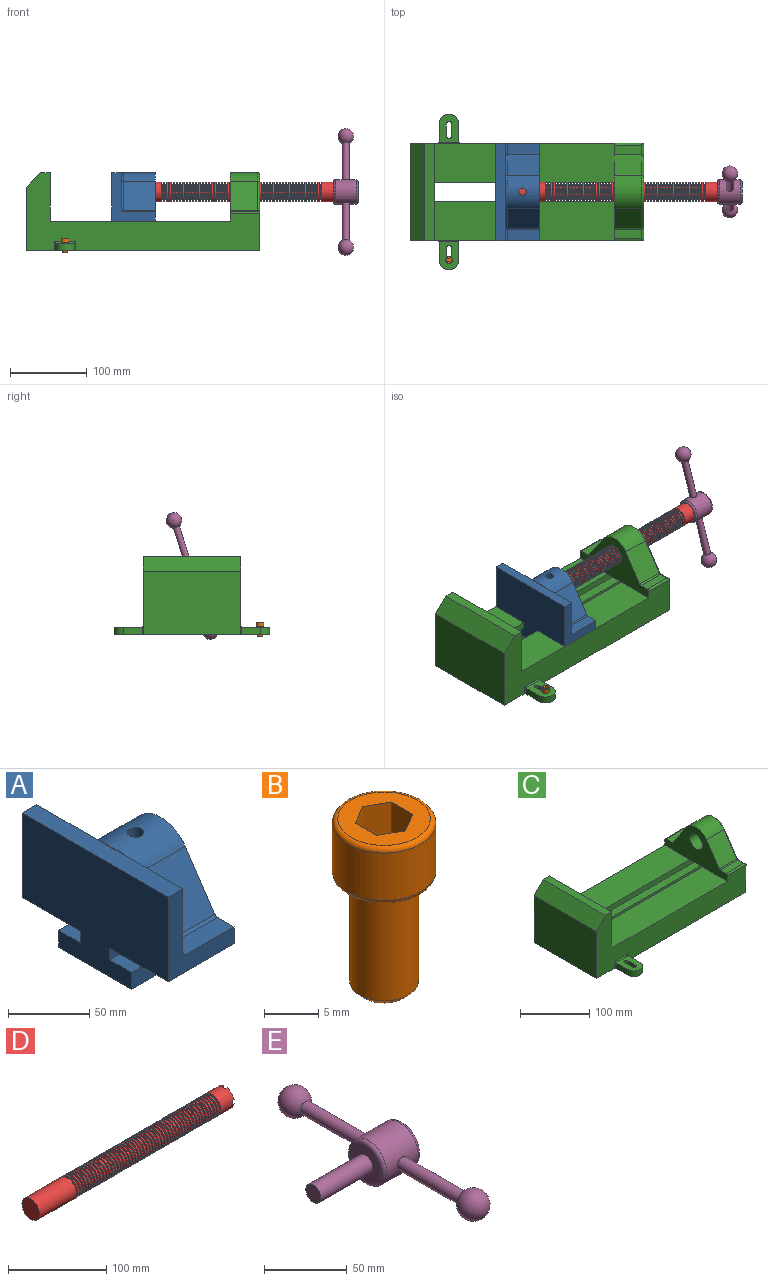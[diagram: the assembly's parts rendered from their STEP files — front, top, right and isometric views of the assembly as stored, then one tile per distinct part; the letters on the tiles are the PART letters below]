
ASSEMBLY  parts=5 mates=5
PART A: 36 faces, bbox 57.2x127x89 mm
  f0: plane 57.15x50.8mm, normal (0,0,-1), area 2903.2mm2, adj f6,f9,f10,f23
  f1: cylinder r=12.7mm len=44.45mm, axis (1,0,0), area 3464.3mm2, adj f6,f15,f16
  f2: plane 41.91x14.52mm, normal (0,0,1), area 608.5mm2, adj f6,f11,f24,f25
  f3: plane 51.86x48.26mm, normal (1,0,0), area 1495.7mm2, adj f8,f10,f31,f33,f35
  f4: plane 51.86x48.26mm, normal (1,0,0), area 1495.7mm2, adj f8,f11,f24,f28,f29
  f5: plane 57.15x50.8mm, normal (0,0,-1), area 2903.2mm2, adj f6,f9,f11,f22
  f6: plane 127x85.09mm, normal (1,0,0), area 5190.6mm2, adj f0,f1,f2,f5,f7,f10,f11,f12
  f7: plane 41.91x14.52mm, normal (0,0,1), area 608.5mm2, adj f6,f10,f30,f31
  f8: plane 127x12.7mm, normal (0,0,1), area 1612.9mm2, adj f3,f4,f9,f10,f11,f26,f34
  f9: plane 127x85.09mm, normal (-1,0,0), area 9096.8mm2, adj f0,f5,f8,f10,f11,f17,f18,f19
  f10: plane 63.5x57.15mm, normal (0,-1,0), area 1372.3mm2, adj f0,f3,f6,f7,f8,f9,f31
  f11: plane 63.5x57.15mm, normal (0,1,0), area 1372.3mm2, adj f2,f4,f5,f6,f8,f9,f24
  f12: plane 41.91x38.43mm, normal (0,-0.83,0.56), area 1939.2mm2, adj f6,f13,f30,f33
  f13: cylinder r=25.4mm len=44.45mm, axis (1,0,0), area 2026.5mm2, adj f6,f12,f14,f16,f26,f28,f34,f35
  f14: plane 41.91x38.43mm, normal (0,0.83,0.56), area 1939.2mm2, adj f6,f13,f25,f29
  f15: plane 25.4x25.4mm, normal (1,0,0), area 506.7mm2, adj f1
  f16: cylinder r=5.08mm len=13.76mm, axis (0,0,1), area 414mm2, adj f1,f13
  f17: plane 57.15x19.05mm, normal (0,0,1), area 1088.7mm2, adj f6,f9,f18,f23
  f18: plane 57.15x12.7mm, normal (0,-1,0), area 725.8mm2, adj f6,f9,f17,f19
  f19: plane 63.5x57.15mm, normal (0,0,-1), area 3629mm2, adj f6,f9,f18,f20
  f20: plane 57.15x12.7mm, normal (0,1,0), area 725.8mm2, adj f6,f9,f19,f21
  f21: plane 57.15x19.05mm, normal (0,0,1), area 1088.7mm2, adj f6,f9,f20,f22
  f22: plane 57.15x8.89mm, normal (0,1,0), area 508.1mm2, adj f5,f6,f9,f21
  f23: plane 57.15x8.89mm, normal (0,-1,0), area 508.1mm2, adj f0,f6,f9,f17
  f24: cylinder r=2.54mm len=14.52mm, axis (0,-1,0), area 57.9mm2, adj f2,f4,f11,f27
  f25: cylinder r=2.54mm len=41.91mm, axis (1,0,0), area 104.3mm2, adj f2,f6,f14,f27
  f26: bspline ~12.24x2.8mm, area 20.9mm2, adj f8,f13,f28
  f27: sphere r=2.54mm, area 6.3mm2, adj f24,f25,f29
  f28: torus R=27.94mm, axis (1,0,0), area 57.8mm2, adj f4,f13,f26,f29
  f29: cylinder r=2.54mm len=39.84mm, axis (0,-0.56,0.83), area 184.6mm2, adj f4,f14,f27,f28
  f30: cylinder r=2.54mm len=41.91mm, axis (1,0,0), area 104.3mm2, adj f6,f7,f12,f32
  f31: cylinder r=2.54mm len=14.52mm, axis (0,-1,0), area 57.9mm2, adj f3,f7,f10,f32
  f32: sphere r=2.54mm, area 6.3mm2, adj f30,f31,f33
  f33: cylinder r=2.54mm len=39.84mm, axis (0,-0.56,-0.83), area 184.6mm2, adj f3,f12,f32,f35
  f34: bspline ~12.24x2.8mm, area 20.9mm2, adj f8,f13,f35
  f35: torus R=27.94mm, axis (1,0,0), area 57.8mm2, adj f3,f13,f33,f34
PART B: 15 faces, bbox 10.3x10.3x19.1 mm
  f0: plane 8.51x8.51mm, normal (0,0,1), area 37.2mm2, adj f5,f6,f7,f8,f9,f10,f14
  f1: cylinder r=3.17mm len=11.94mm, axis (0,0,1), area 238.2mm2, adj f4,f12
  f2: plane 4.83x4.83mm, normal (0,0,-1), area 18.3mm2, adj f12
  f3: cylinder r=4.76mm len=9.53mm, axis (0,0,-1), area 159.6mm2, adj f13,f14
  f4: plane 8.51x8.51mm, normal (0,0,-1), area 25.2mm2, adj f1,f13
  f5: plane 4.83x2.38mm, normal (-0.5,-0.87,0), area 13.3mm2, adj f0,f6,f10,f11
  f6: plane 4.83x2.38mm, normal (0.5,-0.87,0), area 13.3mm2, adj f0,f5,f7,f11
  f7: plane 4.83x2.75mm, normal (1,0,0), area 13.3mm2, adj f0,f6,f8,f11
  f8: plane 4.83x2.38mm, normal (0.5,0.87,0), area 13.3mm2, adj f0,f7,f9,f11
  f9: plane 4.83x2.38mm, normal (-0.5,0.87,0), area 13.3mm2, adj f0,f8,f10,f11
  f10: plane 4.83x2.75mm, normal (-1,0,0), area 13.3mm2, adj f0,f5,f9,f11
  f11: plane 5.5x4.76mm, normal (0,0,1), area 19.6mm2, adj f5,f6,f7,f8,f9,f10
  f12: cone r=3.17mm half-angle=45deg, axis (0,0,1), area 18.9mm2, adj f1,f2
  f13: torus R=4.25mm, axis (0,0,1), area 23mm2, adj f3,f4
  f14: torus R=4.25mm, axis (0,0,1), area 23mm2, adj f0,f3
PART C: 61 faces, bbox 304.8x203.2x103.7 mm
  f0: plane 304.8x101.6mm, normal (0,1,0), area 13520.3mm2, adj f3,f4,f5,f6,f7,f8,f9,f16
  f1: plane 304.8x101.6mm, normal (0,-1,0), area 13520.3mm2, adj f2,f3,f5,f6,f7,f8,f9,f16
  f2: plane 234.95x50.8mm, normal (0,0,1), area 11935.5mm2, adj f1,f5,f16,f26
  f3: plane 127x99.06mm, normal (1,0,0), area 7097.5mm2, adj f0,f1,f9,f14,f17,f18,f19,f20
  f4: plane 234.95x50.8mm, normal (0,0,1), area 11935.5mm2, adj f0,f5,f16,f27
  f5: plane 127x101.6mm, normal (1,0,0), area 9516.1mm2, adj f0,f1,f2,f4,f6,f9,f18,f19
  f6: plane 127x12.7mm, normal (0,0,1), area 1612.9mm2, adj f0,f1,f5,f7
  f7: plane 127x19.05mm, normal (-0.71,0,0.71), area 3421.5mm2, adj f0,f1,f6,f8
  f8: plane 127x82.55mm, normal (-1,0,0), area 10483.8mm2, adj f0,f1,f7,f9
  f9: plane 304.8x203.2mm, normal (0,0,-1), area 33298.3mm2, adj f0,f1,f3,f5,f8,f21,f22,f39
  f10: plane 35.56x11.98mm, normal (0,0,1), area 426mm2, adj f16,f28,f29,f30
  f11: plane 38.43x35.56mm, normal (0,0.83,0.56), area 1645.4mm2, adj f12,f16,f29,f32
  f12: cylinder r=25.4mm len=42.19mm, axis (1,0,0), area 1770.2mm2, adj f11,f13,f16,f33
  f13: plane 38.43x35.56mm, normal (0,-0.83,0.56), area 1645.4mm2, adj f12,f16,f34,f35
  f14: cylinder r=12.7mm len=38.1mm, axis (1,0,0), area 3040.2mm2, adj f3,f16
  f15: plane 35.56x11.98mm, normal (0,0,1), area 426mm2, adj f16,f34,f36,f38
  f16: plane 127x63.5mm, normal (-1,0,0), area 4155.5mm2, adj f0,f1,f2,f4,f10,f11,f12,f13
  f17: plane 38.1x25.4mm, normal (0,0,-1), area 967.7mm2, adj f3,f16,f26,f27
  f18: plane 273.05x19.05mm, normal (0,0,-1), area 5201.6mm2, adj f3,f5,f19,f26
  f19: plane 273.05x12.7mm, normal (0,1,0), area 3467.7mm2, adj f3,f5,f18,f20
  f20: plane 273.05x19.05mm, normal (0,0,1), area 5201.6mm2, adj f3,f5,f19,f21
  f21: plane 273.05x16.51mm, normal (0,1,0), area 4508.1mm2, adj f3,f5,f9,f20
  f22: plane 273.05x16.51mm, normal (0,-1,0), area 4508.1mm2, adj f3,f5,f9,f23
  f23: plane 273.05x19.05mm, normal (0,0,1), area 5201.6mm2, adj f3,f5,f22,f24
  f24: plane 273.05x12.7mm, normal (0,-1,0), area 3467.7mm2, adj f3,f5,f23,f25
  f25: plane 273.05x19.05mm, normal (0,0,-1), area 5201.6mm2, adj f3,f5,f24,f27
  f26: plane 273.05x8.89mm, normal (0,1,0), area 2427.4mm2, adj f2,f3,f5,f17,f18
  f27: plane 273.05x8.89mm, normal (0,-1,0), area 2427.4mm2, adj f3,f4,f5,f17,f25
  f28: cylinder r=2.54mm len=38.1mm, axis (1,0,0), area 148.3mm2, adj f0,f10,f16,f30
  f29: cylinder r=2.54mm len=35.56mm, axis (-1,0,0), area 88.5mm2, adj f10,f11,f16,f31
  f30: cylinder r=2.54mm len=14.52mm, axis (0,1,0), area 54.3mm2, adj f3,f10,f28,f31
  f31: torus R=5.08mm, axis (-1,0,0), area 13.5mm2, adj f3,f29,f30,f32
  f32: cylinder r=2.54mm len=39.84mm, axis (0,0.56,-0.83), area 184.6mm2, adj f3,f11,f31,f33
  f33: torus R=22.86mm, axis (-1,0,0), area 191.4mm2, adj f3,f12,f32,f35
  f34: cylinder r=2.54mm len=35.56mm, axis (-1,0,0), area 88.5mm2, adj f13,f15,f16,f37
  f35: cylinder r=2.54mm len=39.84mm, axis (0,0.56,0.83), area 184.6mm2, adj f3,f13,f33,f37
  f36: cylinder r=2.54mm len=38.1mm, axis (-1,0,0), area 148.3mm2, adj f1,f15,f16,f38
  f37: torus R=5.08mm, axis (-1,0,0), area 13.5mm2, adj f3,f34,f35,f38
  f38: cylinder r=2.54mm len=14.52mm, axis (0,1,0), area 54.3mm2, adj f3,f15,f36,f37
  f39: plane 23.88x9.53mm, normal (-1,0,0), area 227.4mm2, adj f9,f45,f46,f60
  f40: plane 23.88x9.53mm, normal (1,0,0), area 227.4mm2, adj f9,f45,f46,f58
  f41: cylinder r=3.3mm len=9.53mm, axis (0,0,-1), area 98.8mm2, adj f9,f42,f44,f46
  f42: plane 15.62x9.53mm, normal (-1,0,0), area 148.8mm2, adj f9,f41,f43,f46
  f43: cylinder r=3.3mm len=9.53mm, axis (0,0,-1), area 98.8mm2, adj f9,f42,f44,f46
  f44: plane 15.62x9.53mm, normal (1,0,0), area 148.8mm2, adj f9,f41,f43,f46
  f45: cylinder r=12.7mm len=25.4mm, axis (0,0,-1), area 380mm2, adj f9,f39,f40,f46
  f46: plane 36.58x25.4mm, normal (0,0,1), area 722.4mm2, adj f39,f40,f41,f42,f43,f44,f45,f59
  f47: plane 23.88x9.53mm, normal (-1,0,0), area 227.4mm2, adj f9,f53,f54,f56
  f48: plane 23.88x9.53mm, normal (1,0,0), area 227.4mm2, adj f9,f53,f54,f55
  f49: cylinder r=3.3mm len=9.53mm, axis (0,0,-1), area 98.8mm2, adj f9,f50,f52,f54
  f50: plane 15.62x9.53mm, normal (-1,0,0), area 148.8mm2, adj f9,f49,f51,f54
  f51: cylinder r=3.3mm len=9.53mm, axis (0,0,-1), area 98.8mm2, adj f9,f50,f52,f54
  f52: plane 15.62x9.53mm, normal (1,0,0), area 148.8mm2, adj f9,f49,f51,f54
  f53: cylinder r=12.7mm len=25.4mm, axis (0,0,-1), area 380mm2, adj f9,f47,f48,f54
  f54: plane 36.58x25.4mm, normal (0,0,1), area 722.4mm2, adj f47,f48,f49,f50,f51,f52,f53,f57
  f55: cylinder r=1.52mm len=11.05mm, axis (0,0,-1), area 24.1mm2, adj f0,f9,f48,f57
  f56: cylinder r=1.52mm len=11.05mm, axis (0,0,1), area 24.1mm2, adj f0,f9,f47,f57
  f57: cylinder r=1.52mm len=28.45mm, axis (1,0,0), area 63.5mm2, adj f0,f54,f55,f56
  f58: cylinder r=1.52mm len=11.05mm, axis (0,0,1), area 24.1mm2, adj f1,f9,f40,f59
  f59: cylinder r=1.52mm len=28.45mm, axis (-1,0,0), area 63.5mm2, adj f1,f46,f58,f60
  f60: cylinder r=1.52mm len=11.05mm, axis (0,0,-1), area 24.1mm2, adj f1,f9,f39,f59
PART D: 220 faces, bbox 279.4x25.4x25.4 mm
  f0: cylinder r=12.7mm len=25.4mm, axis (-1,0,0), area 1468.2mm2, adj f1,f2,f3,f5,f7,f208,f209,f210
  f1: plane 9.9x9.9mm, normal (1,0,0), area 62.3mm2, adj f0,f4,f213,f216
  f2: plane 9.9x9.9mm, normal (1,0,0), area 62.3mm2, adj f0,f4,f210,f218
  f3: plane 9.9x9.9mm, normal (1,0,0), area 62.3mm2, adj f0,f4,f209,f212
  f4: cylinder r=6.35mm len=25.4mm, axis (1,0,0), area 960.3mm2, adj f1,f2,f3,f5,f6,f208,f209,f210
  f5: plane 9.9x9.9mm, normal (1,0,0), area 62.3mm2, adj f0,f4,f215,f217
  f6: plane 12.7x12.7mm, normal (1,0,0), area 126.7mm2, adj f4
  f7: cone r=12.7mm half-angle=76deg, axis (1,0,0), area 188mm2, adj f0,f9
  f8: cone r=10.16mm half-angle=76deg, axis (-1,0,0), area 188mm2, adj f9,f10
  f9: cylinder r=10.16mm len=20.32mm, axis (1,0,0), area 81.1mm2, adj f7,f8
  f10: cylinder r=12.7mm len=25.4mm, axis (-1,0,0), area 131.7mm2, adj f8,f11
  f11: cone r=12.7mm half-angle=76deg, axis (1,0,0), area 188mm2, adj f10,f13
  f12: cone r=10.16mm half-angle=76deg, axis (-1,0,0), area 188mm2, adj f13,f14
  f13: cylinder r=10.16mm len=20.32mm, axis (1,0,0), area 81.1mm2, adj f11,f12
  f14: cylinder r=12.7mm len=25.4mm, axis (-1,0,0), area 131.7mm2, adj f12,f15
  f15: cone r=12.7mm half-angle=76deg, axis (1,0,0), area 188mm2, adj f14,f17
  f16: cone r=10.16mm half-angle=76deg, axis (-1,0,0), area 188mm2, adj f17,f18
  f17: cylinder r=10.16mm len=20.32mm, axis (1,0,0), area 81.1mm2, adj f15,f16
  f18: cylinder r=12.7mm len=25.4mm, axis (-1,0,0), area 131.7mm2, adj f16,f19
  f19: cone r=12.7mm half-angle=76deg, axis (1,0,0), area 188mm2, adj f18,f21
  f20: cone r=10.16mm half-angle=76deg, axis (-1,0,0), area 188mm2, adj f21,f22
  f21: cylinder r=10.16mm len=20.32mm, axis (1,0,0), area 81.1mm2, adj f19,f20
  f22: cylinder r=12.7mm len=25.4mm, axis (-1,0,0), area 131.7mm2, adj f20,f23
  f23: cone r=12.7mm half-angle=76deg, axis (1,0,0), area 188mm2, adj f22,f25
  f24: cone r=10.16mm half-angle=76deg, axis (-1,0,0), area 188mm2, adj f25,f26
  f25: cylinder r=10.16mm len=20.32mm, axis (1,0,0), area 81.1mm2, adj f23,f24
  f26: cylinder r=12.7mm len=25.4mm, axis (-1,0,0), area 131.7mm2, adj f24,f27
  f27: cone r=12.7mm half-angle=76deg, axis (1,0,0), area 188mm2, adj f26,f29
  f28: cone r=10.16mm half-angle=76deg, axis (-1,0,0), area 188mm2, adj f29,f30
  f29: cylinder r=10.16mm len=20.32mm, axis (1,0,0), area 81.1mm2, adj f27,f28
  f30: cylinder r=12.7mm len=25.4mm, axis (-1,0,0), area 131.7mm2, adj f28,f31
  f31: cone r=12.7mm half-angle=76deg, axis (1,0,0), area 188mm2, adj f30,f33
  f32: cone r=10.16mm half-angle=76deg, axis (-1,0,0), area 188mm2, adj f33,f34
  f33: cylinder r=10.16mm len=20.32mm, axis (1,0,0), area 81.1mm2, adj f31,f32
  f34: cylinder r=12.7mm len=25.4mm, axis (-1,0,0), area 131.7mm2, adj f32,f35
  f35: cone r=12.7mm half-angle=76deg, axis (1,0,0), area 188mm2, adj f34,f37
  f36: cone r=10.16mm half-angle=76deg, axis (-1,0,0), area 188mm2, adj f37,f38
  f37: cylinder r=10.16mm len=20.32mm, axis (1,0,0), area 81.1mm2, adj f35,f36
  f38: cylinder r=12.7mm len=25.4mm, axis (-1,0,0), area 131.7mm2, adj f36,f39
  f39: cone r=12.7mm half-angle=76deg, axis (1,0,0), area 188mm2, adj f38,f41
  f40: cone r=10.16mm half-angle=76deg, axis (-1,0,0), area 188mm2, adj f41,f42
  f41: cylinder r=10.16mm len=20.32mm, axis (1,0,0), area 81.1mm2, adj f39,f40
  f42: cylinder r=12.7mm len=25.4mm, axis (-1,0,0), area 131.7mm2, adj f40,f43
  f43: cone r=12.7mm half-angle=76deg, axis (1,0,0), area 188mm2, adj f42,f45
  f44: cone r=10.16mm half-angle=76deg, axis (-1,0,0), area 188mm2, adj f45,f46
  f45: cylinder r=10.16mm len=20.32mm, axis (1,0,0), area 81.1mm2, adj f43,f44
  f46: cylinder r=12.7mm len=25.4mm, axis (-1,0,0), area 131.7mm2, adj f44,f47
  f47: cone r=12.7mm half-angle=76deg, axis (1,0,0), area 188mm2, adj f46,f49
  f48: cone r=10.16mm half-angle=76deg, axis (-1,0,0), area 188mm2, adj f49,f50
  f49: cylinder r=10.16mm len=20.32mm, axis (1,0,0), area 81.1mm2, adj f47,f48
  f50: cylinder r=12.7mm len=25.4mm, axis (-1,0,0), area 131.7mm2, adj f48,f51
  f51: cone r=12.7mm half-angle=76deg, axis (1,0,0), area 188mm2, adj f50,f53
  f52: cone r=10.16mm half-angle=76deg, axis (-1,0,0), area 188mm2, adj f53,f54
  f53: cylinder r=10.16mm len=20.32mm, axis (1,0,0), area 81.1mm2, adj f51,f52
  f54: cylinder r=12.7mm len=25.4mm, axis (-1,0,0), area 131.7mm2, adj f52,f55
  f55: cone r=12.7mm half-angle=76deg, axis (1,0,0), area 188mm2, adj f54,f57
  f56: cone r=10.16mm half-angle=76deg, axis (-1,0,0), area 188mm2, adj f57,f58
  f57: cylinder r=10.16mm len=20.32mm, axis (1,0,0), area 81.1mm2, adj f55,f56
  f58: cylinder r=12.7mm len=25.4mm, axis (-1,0,0), area 131.7mm2, adj f56,f59
  f59: cone r=12.7mm half-angle=76deg, axis (1,0,0), area 188mm2, adj f58,f61
  f60: cone r=10.16mm half-angle=76deg, axis (-1,0,0), area 188mm2, adj f61,f62
  f61: cylinder r=10.16mm len=20.32mm, axis (1,0,0), area 81.1mm2, adj f59,f60
  f62: cylinder r=12.7mm len=25.4mm, axis (-1,0,0), area 131.7mm2, adj f60,f63
  f63: cone r=12.7mm half-angle=76deg, axis (1,0,0), area 188mm2, adj f62,f65
  f64: cone r=10.16mm half-angle=76deg, axis (-1,0,0), area 188mm2, adj f65,f66
  f65: cylinder r=10.16mm len=20.32mm, axis (1,0,0), area 81.1mm2, adj f63,f64
  f66: cylinder r=12.7mm len=25.4mm, axis (-1,0,0), area 131.7mm2, adj f64,f67
  f67: cone r=12.7mm half-angle=76deg, axis (1,0,0), area 188mm2, adj f66,f69
  f68: cone r=10.16mm half-angle=76deg, axis (-1,0,0), area 188mm2, adj f69,f70
  f69: cylinder r=10.16mm len=20.32mm, axis (1,0,0), area 81.1mm2, adj f67,f68
  f70: cylinder r=12.7mm len=25.4mm, axis (-1,0,0), area 131.7mm2, adj f68,f71
  f71: cone r=12.7mm half-angle=76deg, axis (1,0,0), area 188mm2, adj f70,f73
  f72: cone r=10.16mm half-angle=76deg, axis (-1,0,0), area 188mm2, adj f73,f74
  f73: cylinder r=10.16mm len=20.32mm, axis (1,0,0), area 81.1mm2, adj f71,f72
  f74: cylinder r=12.7mm len=25.4mm, axis (-1,0,0), area 131.7mm2, adj f72,f75
  f75: cone r=12.7mm half-angle=76deg, axis (1,0,0), area 188mm2, adj f74,f77
  f76: cone r=10.16mm half-angle=76deg, axis (-1,0,0), area 188mm2, adj f77,f78
  f77: cylinder r=10.16mm len=20.32mm, axis (1,0,0), area 81.1mm2, adj f75,f76
  f78: cylinder r=12.7mm len=25.4mm, axis (-1,0,0), area 131.7mm2, adj f76,f79
  f79: cone r=12.7mm half-angle=76deg, axis (1,0,0), area 188mm2, adj f78,f81
  f80: cone r=10.16mm half-angle=76deg, axis (-1,0,0), area 188mm2, adj f81,f82
  f81: cylinder r=10.16mm len=20.32mm, axis (1,0,0), area 81.1mm2, adj f79,f80
  f82: cylinder r=12.7mm len=25.4mm, axis (-1,0,0), area 131.7mm2, adj f80,f83
  f83: cone r=12.7mm half-angle=76deg, axis (1,0,0), area 188mm2, adj f82,f85
  f84: cone r=10.16mm half-angle=76deg, axis (-1,0,0), area 188mm2, adj f85,f86
  f85: cylinder r=10.16mm len=20.32mm, axis (1,0,0), area 81.1mm2, adj f83,f84
  f86: cylinder r=12.7mm len=25.4mm, axis (-1,0,0), area 131.7mm2, adj f84,f87
  f87: cone r=12.7mm half-angle=76deg, axis (1,0,0), area 188mm2, adj f86,f89
  f88: cone r=10.16mm half-angle=76deg, axis (-1,0,0), area 188mm2, adj f89,f90
  f89: cylinder r=10.16mm len=20.32mm, axis (1,0,0), area 81.1mm2, adj f87,f88
  f90: cylinder r=12.7mm len=25.4mm, axis (-1,0,0), area 131.7mm2, adj f88,f91
  f91: cone r=12.7mm half-angle=76deg, axis (1,0,0), area 188mm2, adj f90,f93
  f92: cone r=10.16mm half-angle=76deg, axis (-1,0,0), area 188mm2, adj f93,f94
  f93: cylinder r=10.16mm len=20.32mm, axis (1,0,0), area 81.1mm2, adj f91,f92
  f94: cylinder r=12.7mm len=25.4mm, axis (-1,0,0), area 131.7mm2, adj f92,f95
  f95: cone r=12.7mm half-angle=76deg, axis (1,0,0), area 188mm2, adj f94,f97
  f96: cone r=10.16mm half-angle=76deg, axis (-1,0,0), area 188mm2, adj f97,f98
  f97: cylinder r=10.16mm len=20.32mm, axis (1,0,0), area 81.1mm2, adj f95,f96
  f98: cylinder r=12.7mm len=25.4mm, axis (-1,0,0), area 131.7mm2, adj f96,f99
  f99: cone r=12.7mm half-angle=76deg, axis (1,0,0), area 188mm2, adj f98,f101
  f100: cone r=10.16mm half-angle=76deg, axis (-1,0,0), area 188mm2, adj f101,f102
  f101: cylinder r=10.16mm len=20.32mm, axis (1,0,0), area 81.1mm2, adj f99,f100
  f102: cylinder r=12.7mm len=25.4mm, axis (-1,0,0), area 131.7mm2, adj f100,f103
  f103: cone r=12.7mm half-angle=76deg, axis (1,0,0), area 188mm2, adj f102,f105
  f104: cone r=10.16mm half-angle=76deg, axis (-1,0,0), area 188mm2, adj f105,f106
  f105: cylinder r=10.16mm len=20.32mm, axis (1,0,0), area 81.1mm2, adj f103,f104
  f106: cylinder r=12.7mm len=25.4mm, axis (-1,0,0), area 131.7mm2, adj f104,f107
  f107: cone r=12.7mm half-angle=76deg, axis (1,0,0), area 188mm2, adj f106,f109
  f108: cone r=10.16mm half-angle=76deg, axis (-1,0,0), area 188mm2, adj f109,f110
  f109: cylinder r=10.16mm len=20.32mm, axis (1,0,0), area 81.1mm2, adj f107,f108
  f110: cylinder r=12.7mm len=25.4mm, axis (-1,0,0), area 131.7mm2, adj f108,f111
  f111: cone r=12.7mm half-angle=76deg, axis (1,0,0), area 188mm2, adj f110,f113
  f112: cone r=10.16mm half-angle=76deg, axis (-1,0,0), area 188mm2, adj f113,f114
  f113: cylinder r=10.16mm len=20.32mm, axis (1,0,0), area 81.1mm2, adj f111,f112
  f114: cylinder r=12.7mm len=25.4mm, axis (-1,0,0), area 131.7mm2, adj f112,f115
  f115: cone r=12.7mm half-angle=76deg, axis (1,0,0), area 188mm2, adj f114,f117
  f116: cone r=10.16mm half-angle=76deg, axis (-1,0,0), area 188mm2, adj f117,f118
  f117: cylinder r=10.16mm len=20.32mm, axis (1,0,0), area 81.1mm2, adj f115,f116
  f118: cylinder r=12.7mm len=25.4mm, axis (-1,0,0), area 131.7mm2, adj f116,f119
  f119: cone r=12.7mm half-angle=76deg, axis (1,0,0), area 188mm2, adj f118,f121
  f120: cone r=10.16mm half-angle=76deg, axis (-1,0,0), area 188mm2, adj f121,f122
  f121: cylinder r=10.16mm len=20.32mm, axis (1,0,0), area 81.1mm2, adj f119,f120
  f122: cylinder r=12.7mm len=25.4mm, axis (-1,0,0), area 131.7mm2, adj f120,f123
  f123: cone r=12.7mm half-angle=76deg, axis (1,0,0), area 188mm2, adj f122,f125
  f124: cone r=10.16mm half-angle=76deg, axis (-1,0,0), area 188mm2, adj f125,f126
  f125: cylinder r=10.16mm len=20.32mm, axis (1,0,0), area 81.1mm2, adj f123,f124
  f126: cylinder r=12.7mm len=25.4mm, axis (-1,0,0), area 131.7mm2, adj f124,f127
  f127: cone r=12.7mm half-angle=76deg, axis (1,0,0), area 188mm2, adj f126,f129
  f128: cone r=10.16mm half-angle=76deg, axis (-1,0,0), area 188mm2, adj f129,f130
  f129: cylinder r=10.16mm len=20.32mm, axis (1,0,0), area 81.1mm2, adj f127,f128
  f130: cylinder r=12.7mm len=25.4mm, axis (-1,0,0), area 131.7mm2, adj f128,f131
  f131: cone r=12.7mm half-angle=76deg, axis (1,0,0), area 188mm2, adj f130,f133
  f132: cone r=10.16mm half-angle=76deg, axis (-1,0,0), area 188mm2, adj f133,f134
  f133: cylinder r=10.16mm len=20.32mm, axis (1,0,0), area 81.1mm2, adj f131,f132
  f134: cylinder r=12.7mm len=25.4mm, axis (-1,0,0), area 131.7mm2, adj f132,f135
  f135: cone r=12.7mm half-angle=76deg, axis (1,0,0), area 188mm2, adj f134,f137
  f136: cone r=10.16mm half-angle=76deg, axis (-1,0,0), area 188mm2, adj f137,f138
  f137: cylinder r=10.16mm len=20.32mm, axis (1,0,0), area 81.1mm2, adj f135,f136
  f138: cylinder r=12.7mm len=25.4mm, axis (-1,0,0), area 131.7mm2, adj f136,f139
  f139: cone r=12.7mm half-angle=76deg, axis (1,0,0), area 188mm2, adj f138,f141
  f140: cone r=10.16mm half-angle=76deg, axis (-1,0,0), area 188mm2, adj f141,f142
  f141: cylinder r=10.16mm len=20.32mm, axis (1,0,0), area 81.1mm2, adj f139,f140
  f142: cylinder r=12.7mm len=25.4mm, axis (-1,0,0), area 131.7mm2, adj f140,f143
  f143: cone r=12.7mm half-angle=76deg, axis (1,0,0), area 188mm2, adj f142,f145
  f144: cone r=10.16mm half-angle=76deg, axis (-1,0,0), area 188mm2, adj f145,f146
  f145: cylinder r=10.16mm len=20.32mm, axis (1,0,0), area 81.1mm2, adj f143,f144
  f146: cylinder r=12.7mm len=25.4mm, axis (-1,0,0), area 131.7mm2, adj f144,f147
  f147: cone r=12.7mm half-angle=76deg, axis (1,0,0), area 188mm2, adj f146,f149
  f148: cone r=10.16mm half-angle=76deg, axis (-1,0,0), area 188mm2, adj f149,f150
  f149: cylinder r=10.16mm len=20.32mm, axis (1,0,0), area 81.1mm2, adj f147,f148
  f150: cylinder r=12.7mm len=25.4mm, axis (-1,0,0), area 131.7mm2, adj f148,f151
  f151: cone r=12.7mm half-angle=76deg, axis (1,0,0), area 188mm2, adj f150,f153
  f152: cone r=10.16mm half-angle=76deg, axis (-1,0,0), area 188mm2, adj f153,f154
  f153: cylinder r=10.16mm len=20.32mm, axis (1,0,0), area 81.1mm2, adj f151,f152
  f154: cylinder r=12.7mm len=25.4mm, axis (-1,0,0), area 131.7mm2, adj f152,f155
  f155: cone r=12.7mm half-angle=76deg, axis (1,0,0), area 188mm2, adj f154,f157
  f156: cone r=10.16mm half-angle=76deg, axis (-1,0,0), area 188mm2, adj f157,f158
  f157: cylinder r=10.16mm len=20.32mm, axis (1,0,0), area 81.1mm2, adj f155,f156
  f158: cylinder r=12.7mm len=25.4mm, axis (-1,0,0), area 131.7mm2, adj f156,f159
  f159: cone r=12.7mm half-angle=76deg, axis (1,0,0), area 188mm2, adj f158,f161
  f160: cone r=10.16mm half-angle=76deg, axis (-1,0,0), area 188mm2, adj f161,f162
  f161: cylinder r=10.16mm len=20.32mm, axis (1,0,0), area 81.1mm2, adj f159,f160
  f162: cylinder r=12.7mm len=25.4mm, axis (-1,0,0), area 131.7mm2, adj f160,f163
  f163: cone r=12.7mm half-angle=76deg, axis (1,0,0), area 188mm2, adj f162,f165
  f164: cone r=10.16mm half-angle=76deg, axis (-1,0,0), area 188mm2, adj f165,f166
  f165: cylinder r=10.16mm len=20.32mm, axis (1,0,0), area 81.1mm2, adj f163,f164
  f166: cylinder r=12.7mm len=25.4mm, axis (-1,0,0), area 131.7mm2, adj f164,f167
  f167: cone r=12.7mm half-angle=76deg, axis (1,0,0), area 188mm2, adj f166,f169
  f168: cone r=10.16mm half-angle=76deg, axis (-1,0,0), area 188mm2, adj f169,f170
  f169: cylinder r=10.16mm len=20.32mm, axis (1,0,0), area 81.1mm2, adj f167,f168
  f170: cylinder r=12.7mm len=25.4mm, axis (-1,0,0), area 131.7mm2, adj f168,f171
  f171: cone r=12.7mm half-angle=76deg, axis (1,0,0), area 188mm2, adj f170,f173
  f172: cone r=10.16mm half-angle=76deg, axis (-1,0,0), area 188mm2, adj f173,f174
  f173: cylinder r=10.16mm len=20.32mm, axis (1,0,0), area 81.1mm2, adj f171,f172
  f174: cylinder r=12.7mm len=25.4mm, axis (-1,0,0), area 131.7mm2, adj f172,f175
  f175: cone r=12.7mm half-angle=76deg, axis (1,0,0), area 188mm2, adj f174,f177
  f176: cone r=10.16mm half-angle=76deg, axis (-1,0,0), area 188mm2, adj f177,f178
  f177: cylinder r=10.16mm len=20.32mm, axis (1,0,0), area 81.1mm2, adj f175,f176
  f178: cylinder r=12.7mm len=25.4mm, axis (-1,0,0), area 131.7mm2, adj f176,f179
  f179: cone r=12.7mm half-angle=76deg, axis (1,0,0), area 188mm2, adj f178,f181
  f180: cone r=10.16mm half-angle=76deg, axis (-1,0,0), area 188mm2, adj f181,f182
  f181: cylinder r=10.16mm len=20.32mm, axis (1,0,0), area 81.1mm2, adj f179,f180
  f182: cylinder r=12.7mm len=25.4mm, axis (-1,0,0), area 131.7mm2, adj f180,f183
  f183: cone r=12.7mm half-angle=76deg, axis (1,0,0), area 188mm2, adj f182,f185
  f184: cone r=10.16mm half-angle=76deg, axis (-1,0,0), area 188mm2, adj f185,f186
  f185: cylinder r=10.16mm len=20.32mm, axis (1,0,0), area 81.1mm2, adj f183,f184
  f186: cylinder r=12.7mm len=25.4mm, axis (-1,0,0), area 131.7mm2, adj f184,f187
  f187: cone r=12.7mm half-angle=76deg, axis (1,0,0), area 188mm2, adj f186,f189
  f188: cone r=10.16mm half-angle=76deg, axis (-1,0,0), area 188mm2, adj f189,f190
  f189: cylinder r=10.16mm len=20.32mm, axis (1,0,0), area 81.1mm2, adj f187,f188
  f190: cylinder r=12.7mm len=25.4mm, axis (-1,0,0), area 131.7mm2, adj f188,f191
  f191: cone r=12.7mm half-angle=76deg, axis (1,0,0), area 188mm2, adj f190,f193
  f192: cone r=10.16mm half-angle=76deg, axis (-1,0,0), area 188mm2, adj f193,f194
  f193: cylinder r=10.16mm len=20.32mm, axis (1,0,0), area 81.1mm2, adj f191,f192
  f194: cylinder r=12.7mm len=25.4mm, axis (-1,0,0), area 131.7mm2, adj f192,f195
  f195: cone r=12.7mm half-angle=76deg, axis (1,0,0), area 188mm2, adj f194,f197
  f196: cone r=10.16mm half-angle=76deg, axis (-1,0,0), area 188mm2, adj f197,f198
  f197: cylinder r=10.16mm len=20.32mm, axis (1,0,0), area 81.1mm2, adj f195,f196
  f198: cylinder r=12.7mm len=25.4mm, axis (-1,0,0), area 131.7mm2, adj f196,f199
  f199: cone r=12.7mm half-angle=76deg, axis (1,0,0), area 188mm2, adj f198,f201
  f200: cone r=10.16mm half-angle=76deg, axis (-1,0,0), area 188mm2, adj f201,f202
  f201: cylinder r=10.16mm len=20.32mm, axis (1,0,0), area 81.1mm2, adj f199,f200
  f202: cylinder r=12.7mm len=25.4mm, axis (-1,0,0), area 131.7mm2, adj f200,f203
  f203: cone r=12.7mm half-angle=76deg, axis (1,0,0), area 188mm2, adj f202,f205
  f204: cone r=10.16mm half-angle=76deg, axis (-1,0,0), area 188mm2, adj f205,f207
  f205: cylinder r=10.16mm len=20.32mm, axis (1,0,0), area 81.1mm2, adj f203,f204
  f206: plane 25.4x25.4mm, normal (-1,0,0), area 506.7mm2, adj f207
  f207: cylinder r=12.7mm len=52.45mm, axis (-1,0,0), area 4185.4mm2, adj f204,f206
  f208: plane 6.88x5.08mm, normal (1,0,0), area 32.7mm2, adj f0,f4,f209,f210
  f209: plane 6.62x2.54mm, normal (0,-1,0), area 16.8mm2, adj f0,f3,f4,f208
  f210: plane 6.62x2.54mm, normal (0,1,0), area 16.8mm2, adj f0,f2,f4,f208
  f211: plane 6.88x5.08mm, normal (1,0,0), area 32.7mm2, adj f0,f4,f212,f213
  f212: plane 6.62x2.54mm, normal (0,0,1), area 16.8mm2, adj f0,f3,f4,f211
  f213: plane 6.62x2.54mm, normal (0,0,-1), area 16.8mm2, adj f0,f1,f4,f211
  f214: plane 6.88x5.08mm, normal (1,0,0), area 32.7mm2, adj f0,f4,f215,f216
  f215: plane 6.62x2.54mm, normal (0,1,0), area 16.8mm2, adj f0,f4,f5,f214
  f216: plane 6.62x2.54mm, normal (0,-1,0), area 16.8mm2, adj f0,f1,f4,f214
  f217: plane 6.62x2.54mm, normal (0,0,-1), area 16.8mm2, adj f0,f4,f5,f219
  f218: plane 6.62x2.54mm, normal (0,0,1), area 16.8mm2, adj f0,f2,f4,f219
  f219: plane 6.88x5.08mm, normal (1,0,0), area 32.7mm2, adj f0,f4,f217,f218
PART E: 11 faces, bbox 76.2x172.7x34.4 mm
  f0: sphere r=10.16mm, area 1231.8mm2, adj f1
  f1: cylinder r=4.45mm len=51.82mm, axis (0,1,0), area 1438.5mm2, adj f0,f4
  f2: sphere r=10.16mm, area 1231.8mm2, adj f3
  f3: cylinder r=4.45mm len=51.82mm, axis (0,1,0), area 1438.5mm2, adj f2,f4
  f4: cylinder r=15.88mm len=31.75mm, axis (-1,0,0), area 2534.7mm2, adj f1,f3,f9,f10
  f5: cylinder r=6.35mm len=44.45mm, axis (-1,0,0), area 1773.5mm2, adj f6,f8
  f6: plane 12.7x12.7mm, normal (-1,0,0), area 126.7mm2, adj f5
  f7: plane 26.67x26.67mm, normal (1,0,0), area 558.6mm2, adj f10
  f8: plane 26.67x26.67mm, normal (-1,0,0), area 432mm2, adj f5,f9
  f9: torus R=13.33mm, axis (1,0,0), area 374.8mm2, adj f4,f8
  f10: torus R=13.33mm, axis (1,0,0), area 374.8mm2, adj f4,f7
PLACE A t=(80.01,0,0)mm
PLACE B rot(axis=(0,0,1),90deg) t=(-254,-88.9,9.52)mm
PLACE C at identity fixed
PLACE D rot(axis=(1,0,0),72deg) t=(80.01,72.47,52.65)mm
PLACE E rot(axis=(1,0,0),72deg) t=(58.42,72.47,52.65)mm
MATE fastened D.f4 <-> E.f5  axis (1,0,0) through (96.52,0,76.2)mm
MATE planar A.f0 <-> C.f2  axis (0,0,-1) through (-164.47,-38.1,38.1)mm
MATE pin_slot B.f1 <-> C.f41  axis (0,0,1) through (-254,-88.9,9.52)mm
MATE revolute D.f7 <-> A.f28  axis (-1,0,0) through (-180.34,0,76.2)mm
MATE cylindrical C.f12 <-> D.f7  axis (-1,0,0) through (-38.1,0,76.2)mm
